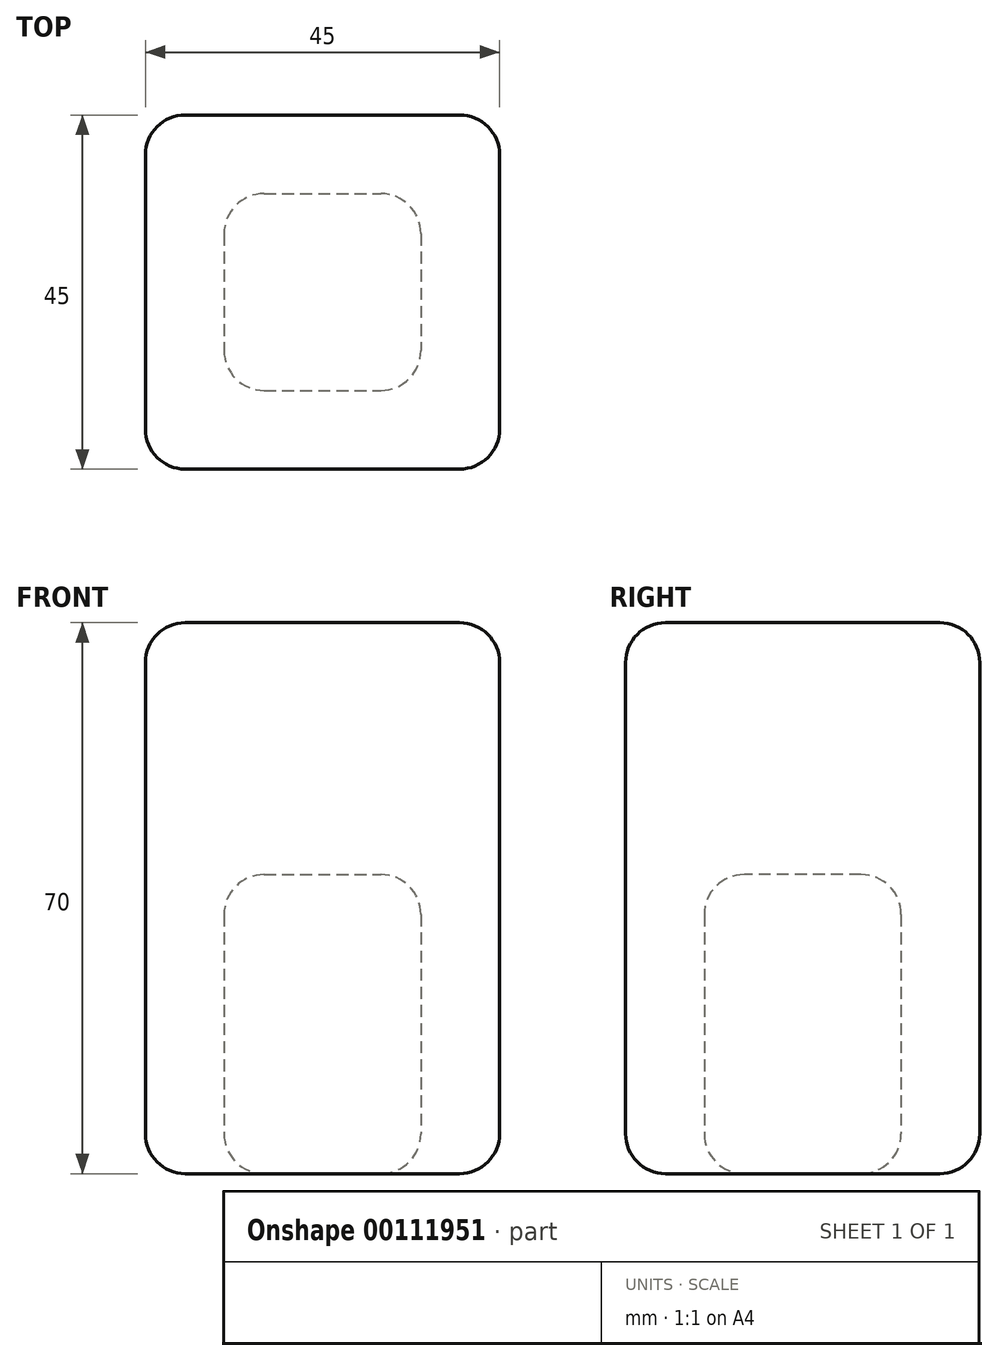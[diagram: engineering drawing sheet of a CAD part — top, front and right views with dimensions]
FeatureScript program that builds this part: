
annotation { "Feature Type Name" : "Feature", "Feature Type Description" : "" }
export const myFeature = defineFeature(function(context is Context, id is Id, definition is map)
    precondition{}
    {
        {
            var Q0;
            Q0=qCreatedBy(makeId("Top.planeOp"),FACE);
            var sketch = newSketch(context, id + "F0", { "sketchPlane" : qUnion([Q0])});
            skLineSegment(sketch, "E0.bottom", {"start": v(22.5, -22.5) * mm, "end": v(-22.5, -22.5) * mm});
            skLineSegment(sketch, "E0.top", {"start": v(22.5, 22.5) * mm, "end": v(-22.5, 22.5) * mm});
            skLineSegment(sketch, "E0.left", {"start": v(22.5, -22.5) * mm, "end": v(22.5, 22.5) * mm});
            skLineSegment(sketch, "E0.right", {"start": v(-22.5, -22.5) * mm, "end": v(-22.5, 22.5) * mm});
            skPoint(sketch, "E0.middle", {"position": v(0, 0) * mm});
            skSolve(sketch);
        }
        {
            var Q0;
            Q0 = qSketchRegion(id + "F0", true);
            extrude(context, id + "F1", {"entities" : qUnion([Q0]), "depth" : 70 * mm});
        }
        {
            var Q0;
            Q0=makeQuery(id+"F1.opExtrude","CAP_EDGE",EDGE,{"disambiguationData":[OSD([sQuery(id+"F0.wireOp",EDGE,"E0.bottom")])],"isStart":false});
            var Q1;
            Q1=makeQuery(id+"F1.opExtrude","CAP_EDGE",EDGE,{"disambiguationData":[OSD([sQuery(id+"F0.wireOp",EDGE,"E0.right")])],"isStart":false});
            var Q2;
            Q2=makeQuery(id+"F1.opExtrude","CAP_EDGE",EDGE,{"disambiguationData":[OSD([sQuery(id+"F0.wireOp",EDGE,"E0.top")])],"isStart":false});
            var Q3;
            Q3=makeQuery(id+"F1.opExtrude","CAP_EDGE",EDGE,{"disambiguationData":[OSD([sQuery(id+"F0.wireOp",EDGE,"E0.left")])],"isStart":false});
            var Q4;
            Q4=makeQuery(id+"F1.opExtrude","SWEPT_EDGE",EDGE,{"disambiguationData":[OSD([sQuery(id+"F0.wireOp",EDGE,"E0.bottom"),sQuery(id+"F0.wireOp",EDGE,"E0.left")])]});
            var Q5;
            Q5=makeQuery(id+"F1.opExtrude","SWEPT_EDGE",EDGE,{"disambiguationData":[OSD([sQuery(id+"F0.wireOp",EDGE,"E0.top"),sQuery(id+"F0.wireOp",EDGE,"E0.left")])]});
            var Q6;
            Q6=makeQuery(id+"F1.opExtrude","SWEPT_EDGE",EDGE,{"disambiguationData":[OSD([sQuery(id+"F0.wireOp",EDGE,"E0.bottom"),sQuery(id+"F0.wireOp",EDGE,"E0.right")])]});
            var Q7;
            Q7=makeQuery(id+"F1.opExtrude","CAP_EDGE",EDGE,{"disambiguationData":[OSD([sQuery(id+"F0.wireOp",EDGE,"E0.bottom")])],"isStart":true});
            var Q8;
            Q8=makeQuery(id+"F1.opExtrude","CAP_EDGE",EDGE,{"disambiguationData":[OSD([sQuery(id+"F0.wireOp",EDGE,"E0.left")])],"isStart":true});
            var Q9;
            Q9=makeQuery(id+"F1.opExtrude","CAP_EDGE",EDGE,{"disambiguationData":[OSD([sQuery(id+"F0.wireOp",EDGE,"E0.right")])],"isStart":true});
            var Q10;
            Q10=makeQuery(id+"F1.opExtrude","SWEPT_EDGE",EDGE,{"disambiguationData":[OSD([sQuery(id+"F0.wireOp",EDGE,"E0.top"),sQuery(id+"F0.wireOp",EDGE,"E0.right")])]});
            var Q11;
            Q11=makeQuery(id+"F1.opExtrude","CAP_EDGE",EDGE,{"disambiguationData":[OSD([sQuery(id+"F0.wireOp",EDGE,"E0.top")])],"isStart":true});
            fillet(context, id + "F2", {"entities" : qUnion([Q0, Q1, Q2, Q3, Q4, Q5, Q6, Q7, Q8, Q9, Q10, Q11]), "radius" : 5.08 * mm, "tangentPropagation" : true, "allowEdgeOverflow" : false});
        }
        {
            var Q0;
            Q0=qCreatedBy(makeId("Top.planeOp"),FACE);
            var sketch = newSketch(context, id + "F3", { "sketchPlane" : qUnion([Q0])});
            skLineSegment(sketch, "E1.bottom", {"start": v(-12.5, 12.5) * mm, "end": v(12.5, 12.5) * mm});
            skLineSegment(sketch, "E1.top", {"start": v(-12.5, -12.5) * mm, "end": v(12.5, -12.5) * mm});
            skLineSegment(sketch, "E1.left", {"start": v(-12.5, 12.5) * mm, "end": v(-12.5, -12.5) * mm});
            skLineSegment(sketch, "E1.right", {"start": v(12.5, 12.5) * mm, "end": v(12.5, -12.5) * mm});
            skPoint(sketch, "E1.middle", {"position": v(0, 0) * mm});
            skSolve(sketch);
        }
        {
            var Q0;
            Q0 = qSketchRegion(id + "F3", true);
            extrude(context, id + "F4", {"entities" : qUnion([Q0]), "depth" : 38 * mm});
        }
        {
            var Q0;
            Q0=makeQuery(id+"F4.opExtrude","SWEPT_FACE",FACE,{"disambiguationData":[OSD([sQuery(id+"F3.wireOp",EDGE,"E1.right")])]});
            var Q1;
            Q1=makeQuery(id+"F4.opExtrude","CAP_EDGE",EDGE,{"disambiguationData":[OSD([sQuery(id+"F3.wireOp",EDGE,"E1.bottom")])],"isStart":true});
            var Q2;
            Q2=makeQuery(id+"F4.opExtrude","CAP_FACE",FACE,{"disambiguationData":[OSD([sQuery(id+"F3.wireOp",EDGE,"E1.bottom"),sQuery(id+"F3.wireOp",EDGE,"E1.top"),sQuery(id+"F3.wireOp",EDGE,"E1.left"),sQuery(id+"F3.wireOp",EDGE,"E1.right")])],"isStart":false});
            var Q3;
            Q3=makeQuery(id+"F4.opExtrude","CAP_EDGE",EDGE,{"disambiguationData":[OSD([sQuery(id+"F3.wireOp",EDGE,"E1.right")])],"isStart":false});
            var Q4;
            Q4=makeQuery(id+"F4.opExtrude","CAP_EDGE",EDGE,{"disambiguationData":[OSD([sQuery(id+"F3.wireOp",EDGE,"E1.bottom")])],"isStart":false});
            var Q5;
            Q5=makeQuery(id+"F4.opExtrude","CAP_FACE",FACE,{"disambiguationData":[OSD([sQuery(id+"F3.wireOp",EDGE,"E1.bottom"),sQuery(id+"F3.wireOp",EDGE,"E1.top"),sQuery(id+"F3.wireOp",EDGE,"E1.left"),sQuery(id+"F3.wireOp",EDGE,"E1.right")])],"isStart":true});
            var Q6;
            Q6=makeQuery(id+"F4.opExtrude","SWEPT_EDGE",EDGE,{"disambiguationData":[OSD([sQuery(id+"F3.wireOp",EDGE,"E1.bottom"),sQuery(id+"F3.wireOp",EDGE,"E1.right")])]});
            var Q7;
            Q7=makeQuery(id+"F4.opExtrude","SWEPT_FACE",FACE,{"disambiguationData":[OSD([sQuery(id+"F3.wireOp",EDGE,"E1.bottom")])]});
            var Q8;
            Q8=makeQuery(id+"F4.opExtrude","CAP_EDGE",EDGE,{"disambiguationData":[OSD([sQuery(id+"F3.wireOp",EDGE,"E1.left")])],"isStart":false});
            var Q9;
            Q9=makeQuery(id+"F4.opExtrude","CAP_EDGE",EDGE,{"disambiguationData":[OSD([sQuery(id+"F3.wireOp",EDGE,"E1.top")])],"isStart":false});
            var Q10;
            Q10=makeQuery(id+"F4.opExtrude","CAP_EDGE",EDGE,{"disambiguationData":[OSD([sQuery(id+"F3.wireOp",EDGE,"E1.top")])],"isStart":true});
            var Q11;
            Q11=makeQuery(id+"F4.opExtrude","SWEPT_EDGE",EDGE,{"disambiguationData":[OSD([sQuery(id+"F3.wireOp",EDGE,"E1.top"),sQuery(id+"F3.wireOp",EDGE,"E1.right")])]});
            var Q12;
            Q12=makeQuery(id+"F4.opExtrude","SWEPT_EDGE",EDGE,{"disambiguationData":[OSD([sQuery(id+"F3.wireOp",EDGE,"E1.top"),sQuery(id+"F3.wireOp",EDGE,"E1.left")])]});
            var Q13;
            Q13=makeQuery(id+"F4.opExtrude","SWEPT_EDGE",EDGE,{"disambiguationData":[OSD([sQuery(id+"F3.wireOp",EDGE,"E1.bottom"),sQuery(id+"F3.wireOp",EDGE,"E1.left")])]});
            var Q14;
            Q14=makeQuery(id+"F4.opExtrude","CAP_EDGE",EDGE,{"disambiguationData":[OSD([sQuery(id+"F3.wireOp",EDGE,"E1.right")])],"isStart":true});
            var Q15;
            Q15=makeQuery(id+"F4.opExtrude","CAP_EDGE",EDGE,{"disambiguationData":[OSD([sQuery(id+"F3.wireOp",EDGE,"E1.left")])],"isStart":true});
            var Q16;
            Q16=makeQuery(id+"F4.opExtrude","SWEPT_FACE",FACE,{"disambiguationData":[OSD([sQuery(id+"F3.wireOp",EDGE,"E1.left")])]});
            var Q17;
            Q17=makeQuery(id+"F4.opExtrude","SWEPT_FACE",FACE,{"disambiguationData":[OSD([sQuery(id+"F3.wireOp",EDGE,"E1.top")])]});
            fillet(context, id + "F5", {"entities" : qUnion([Q0, Q1, Q2, Q3, Q4, Q5, Q6, Q7, Q8, Q9, Q10, Q11, Q12, Q13, Q14, Q15, Q16, Q17]), "radius" : 5.08 * mm, "tangentPropagation" : true, "allowEdgeOverflow" : false});
        }
    });
